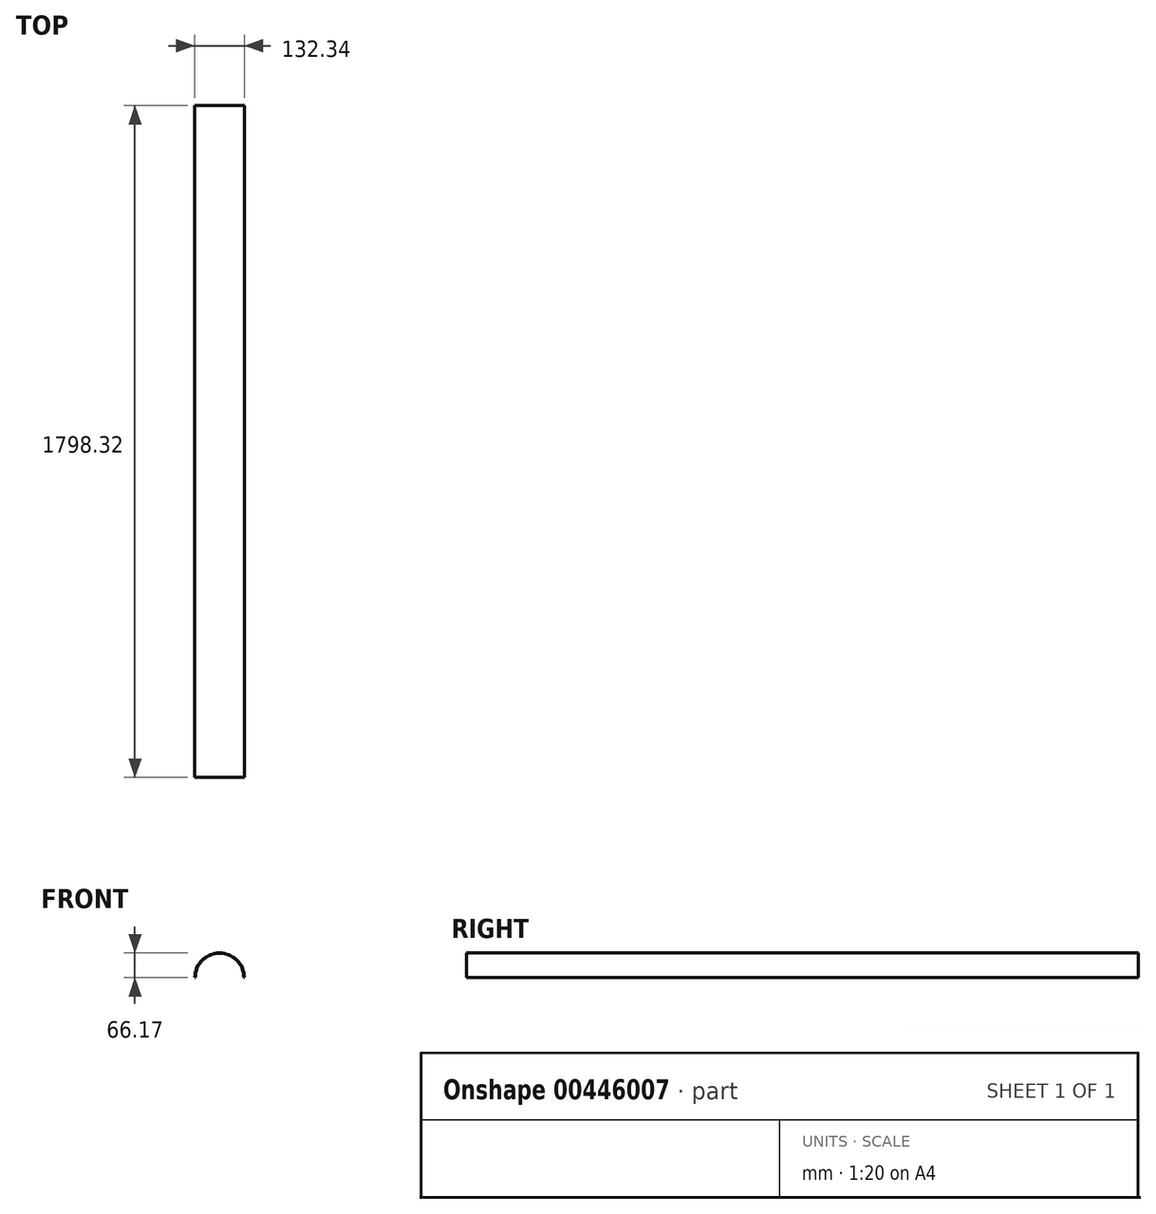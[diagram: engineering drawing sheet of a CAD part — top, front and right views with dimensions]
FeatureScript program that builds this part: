
annotation { "Feature Type Name" : "Feature", "Feature Type Description" : "" }
export const myFeature = defineFeature(function(context is Context, id is Id, definition is map)
    precondition{}
    {
        {
            var Q0;
            Q0=qCreatedBy(makeId("Front.planeOp"),FACE);
            var sketch = newSketch(context, id + "F0", { "sketchPlane" : qUnion([Q0])});
            skArc(sketch, "E0", {"start": v(-65.07, 0) * mm, "mid": v(0, 65.07) * mm, "end": v(65.07, 0) * mm});
            skArc(sketch, "E1.0", {"start": v(-66.17, 0) * mm, "mid": v(0, 66.17) * mm, "end": v(66.17, 0) * mm});
            skLineSegment(sketch, "E2", {"start": v(-65.07, 0) * mm, "end": v(-66.17, 0) * mm});
            skLineSegment(sketch, "E3", {"start": v(66.17, 0) * mm, "end": v(65.07, 0) * mm});
            skSolve(sketch);
        }
        {
            var Q0;
            Q0 = qSketchRegion(id + "F0", true);
            extrude(context, id + "F1", {"entities" : qUnion([Q0]), "oppositeDirection" : true, "depth" : 1798.32 * mm, "offsetDistance" : 25.4 * mm});
        }
    });
